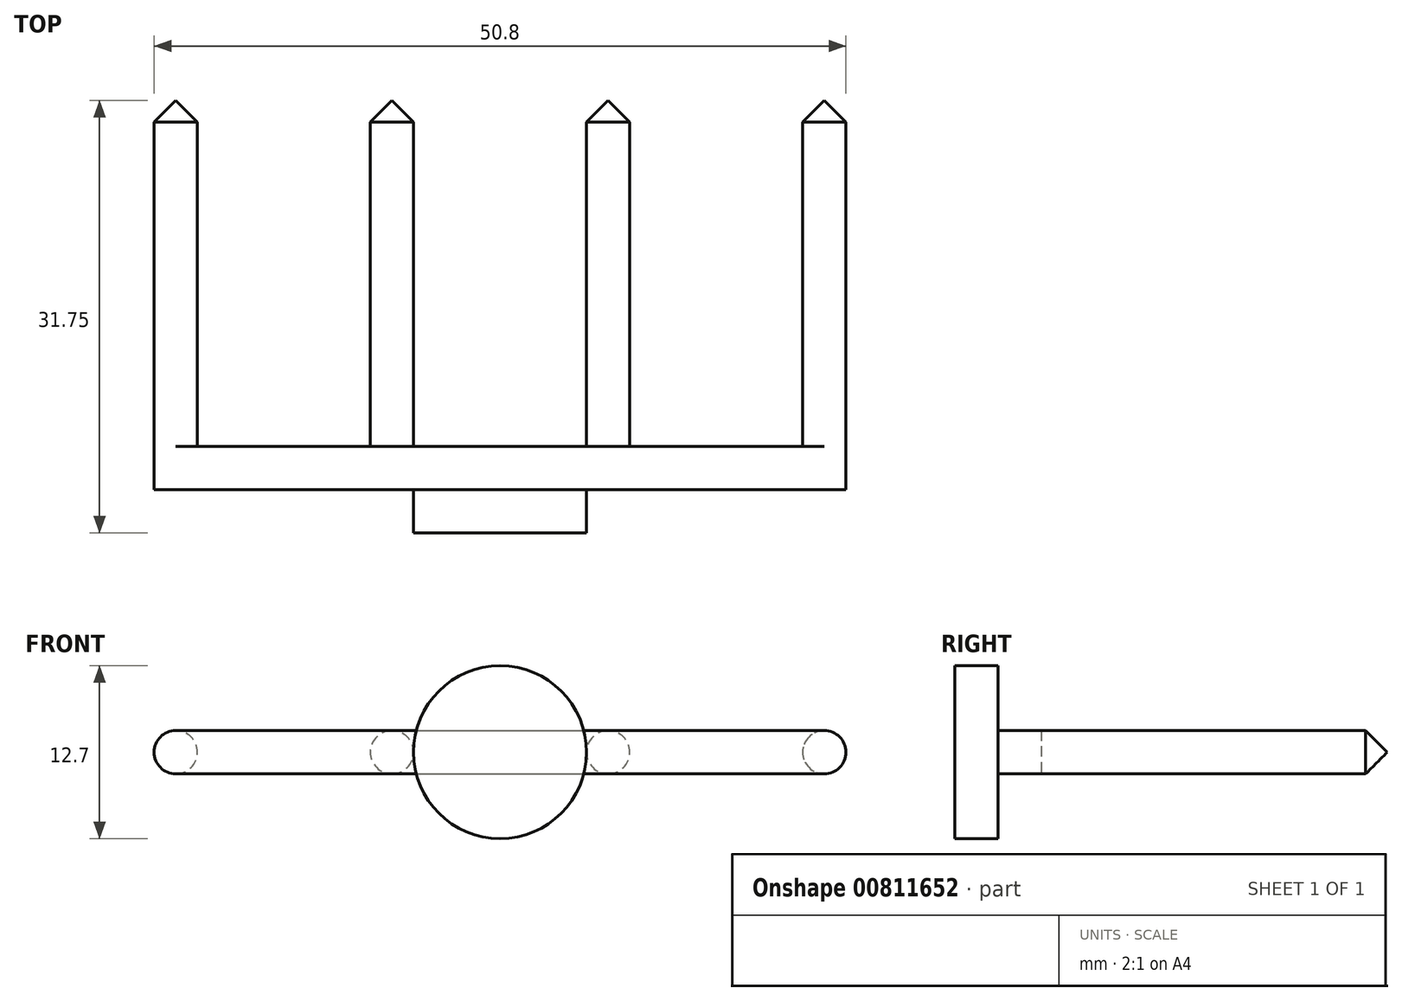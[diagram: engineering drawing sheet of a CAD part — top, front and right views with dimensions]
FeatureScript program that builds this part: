
annotation { "Feature Type Name" : "Feature", "Feature Type Description" : "" }
export const myFeature = defineFeature(function(context is Context, id is Id, definition is map)
    precondition{}
    {
        {
            var Q0;
            Q0=qCreatedBy(makeId("Top.planeOp"),FACE);
            var sketch = newSketch(context, id + "F0", { "sketchPlane" : qUnion([Q0])});
            skLineSegment(sketch, "E0.bottom", {"start": v(-14.88, 23.6) * mm, "end": v(-2.18, 23.6) * mm});
            skLineSegment(sketch, "E0.top", {"start": v(-14.88, 20.43) * mm, "end": v(-2.18, 20.43) * mm});
            skLineSegment(sketch, "E0.left", {"start": v(-14.88, 23.6) * mm, "end": v(-14.88, 20.43) * mm});
            skLineSegment(sketch, "E0.right", {"start": v(-2.18, 23.6) * mm, "end": v(-2.18, 20.43) * mm});
            skLineSegment(sketch, "E1", {"start": v(-2.18, 23.6) * mm, "end": v(16.87, 23.6) * mm});
            skLineSegment(sketch, "E2", {"start": v(-14.88, 23.6) * mm, "end": v(-33.93, 23.6) * mm});
            skLineSegment(sketch, "E3", {"start": v(-33.93, 23.6) * mm, "end": v(-33.93, 26.78) * mm});
            skLineSegment(sketch, "E4", {"start": v(-33.93, 26.78) * mm, "end": v(16.87, 26.78) * mm});
            skLineSegment(sketch, "E5", {"start": v(16.87, 26.78) * mm, "end": v(16.87, 23.6) * mm});
            skLineSegment(sketch, "E6", {"start": v(-33.93, 26.78) * mm, "end": v(-33.93, 52.18) * mm});
            skLineSegment(sketch, "E7", {"start": v(-33.93, 52.18) * mm, "end": v(-30.76, 52.18) * mm});
            skLineSegment(sketch, "E8", {"start": v(-30.76, 52.18) * mm, "end": v(-30.76, 26.78) * mm});
            skLineSegment(sketch, "E9", {"start": v(16.87, 26.78) * mm, "end": v(16.87, 52.18) * mm});
            skLineSegment(sketch, "E10", {"start": v(16.87, 52.18) * mm, "end": v(13.7, 52.18) * mm});
            skLineSegment(sketch, "E11", {"start": v(13.7, 52.18) * mm, "end": v(13.7, 26.78) * mm});
            skLineSegment(sketch, "E12", {"start": v(-30.76, 26.78) * mm, "end": v(-18.06, 26.78) * mm});
            skLineSegment(sketch, "E13", {"start": v(-18.06, 26.78) * mm, "end": v(-18.06, 52.18) * mm});
            skLineSegment(sketch, "E14", {"start": v(-18.06, 52.18) * mm, "end": v(-14.88, 52.18) * mm});
            skLineSegment(sketch, "E15", {"start": v(-14.88, 52.18) * mm, "end": v(-14.88, 26.78) * mm});
            skLineSegment(sketch, "E16", {"start": v(-14.88, 26.78) * mm, "end": v(-8.53, 26.78) * mm});
            skLineSegment(sketch, "E17", {"start": v(-8.53, 26.78) * mm, "end": v(-2.18, 26.78) * mm});
            skLineSegment(sketch, "E18", {"start": v(-2.18, 26.78) * mm, "end": v(-2.18, 52.18) * mm});
            skLineSegment(sketch, "E19", {"start": v(-2.18, 52.18) * mm, "end": v(1, 52.18) * mm});
            skLineSegment(sketch, "E20", {"start": v(1, 52.18) * mm, "end": v(1, 26.78) * mm});
            skLineSegment(sketch, "E21", {"start": v(-8.53, 23.6) * mm, "end": v(-8.53, 20.43) * mm});
            skSolve(sketch);
        }
        {
            var Q0;
            {var subQ0=sQuery(id+"F0.wireOp",EDGE,"E0.left");Q0=makeQuery(id+"F0.imprint","IMPRINT",FACE,{"disambiguationData":[TD([[makeQuery(id+"F0.imprint","IMPRINT",EDGE,{"derivedFrom":subQ0}),1.0]])]});}
            var Q1;
            Q1=sQuery(id+"F0.wireOp",EDGE,"E21");
            revolve(context, id + "F1", {"surfaceOperationType" : NewSurfaceOperationType.NEW, "entities" : qUnion([Q0]), "axis" : qUnion([Q1]), "revolveType" : RevolveType.FULL});
        }
        {
            var Q0;
            {var subQ11=sQuery(id+"F0.wireOp",EDGE,"E1");Q0=makeQuery(id+"F0.imprint","IMPRINT",FACE,{"disambiguationData":[TD([[makeQuery(id+"F0.imprint","IMPRINT",EDGE,{"derivedFrom":subQ11}),1.0]])]});}
            var Q1;
            {var subQ0=sQuery(id+"F0.wireOp",EDGE,"E6");Q1=makeQuery(id+"F0.imprint","IMPRINT",FACE,{"disambiguationData":[TD([[makeQuery(id+"F0.imprint","IMPRINT",EDGE,{"derivedFrom":subQ0}),-1.0]])]});}
            var Q2;
            {var subQ0=sQuery(id+"F0.wireOp",EDGE,"E13");Q2=makeQuery(id+"F0.imprint","IMPRINT",FACE,{"disambiguationData":[TD([[makeQuery(id+"F0.imprint","IMPRINT",EDGE,{"derivedFrom":subQ0}),-1.0]])]});}
            var Q3;
            {var subQ0=sQuery(id+"F0.wireOp",EDGE,"E18");Q3=makeQuery(id+"F0.imprint","IMPRINT",FACE,{"disambiguationData":[TD([[makeQuery(id+"F0.imprint","IMPRINT",EDGE,{"derivedFrom":subQ0}),-1.0]])]});}
            var Q4;
            {var subQ0=sQuery(id+"F0.wireOp",EDGE,"E9");Q4=makeQuery(id+"F0.imprint","IMPRINT",FACE,{"disambiguationData":[TD([[makeQuery(id+"F0.imprint","IMPRINT",EDGE,{"derivedFrom":subQ0}),1.0]])]});}
            extrude(context, id + "F2", {"entities" : qUnion([Q0, Q1, Q2, Q3, Q4]), "operationType" : NewBodyOperationType.ADD, "endBound" : BoundingType.SYMMETRIC, "depth" : 3.17 * mm, "offsetDistance" : 25.4 * mm});
        }
        {
            var Q0;
            Q0=makeQuery(id+"F2.opExtrude","CAP_EDGE",EDGE,{"disambiguationData":[OSD([sQuery(id+"F0.wireOp",EDGE,"E3"),sQuery(id+"F0.wireOp",EDGE,"E6")])],"isStart":false});
            var Q1;
            Q1=makeQuery(id+"F2.opExtrude","CAP_EDGE",EDGE,{"disambiguationData":[OSD([sQuery(id+"F0.wireOp",EDGE,"E3"),sQuery(id+"F0.wireOp",EDGE,"E6")])],"isStart":true});
            var Q2;
            Q2=makeQuery(id+"F2.opExtrude","CAP_EDGE",EDGE,{"disambiguationData":[OSD([sQuery(id+"F0.wireOp",EDGE,"E8")])],"isStart":false});
            var Q3;
            Q3=makeQuery(id+"F2.opExtrude","CAP_EDGE",EDGE,{"disambiguationData":[OSD([sQuery(id+"F0.wireOp",EDGE,"E8")])],"isStart":true});
            var Q4;
            Q4=makeQuery(id+"F2.opExtrude","CAP_EDGE",EDGE,{"disambiguationData":[OSD([sQuery(id+"F0.wireOp",EDGE,"E13")])],"isStart":false});
            var Q5;
            Q5=makeQuery(id+"F2.opExtrude","CAP_EDGE",EDGE,{"disambiguationData":[OSD([sQuery(id+"F0.wireOp",EDGE,"E13")])],"isStart":true});
            var Q6;
            Q6=makeQuery(id+"F2.opExtrude","CAP_EDGE",EDGE,{"disambiguationData":[OSD([sQuery(id+"F0.wireOp",EDGE,"E15")])],"isStart":false});
            var Q7;
            Q7=makeQuery(id+"F2.opExtrude","CAP_EDGE",EDGE,{"disambiguationData":[OSD([sQuery(id+"F0.wireOp",EDGE,"E15")])],"isStart":true});
            var Q8;
            Q8=makeQuery(id+"F2.opExtrude","CAP_EDGE",EDGE,{"disambiguationData":[OSD([sQuery(id+"F0.wireOp",EDGE,"E18")])],"isStart":false});
            var Q9;
            Q9=makeQuery(id+"F2.opExtrude","CAP_EDGE",EDGE,{"disambiguationData":[OSD([sQuery(id+"F0.wireOp",EDGE,"E18")])],"isStart":true});
            var Q10;
            Q10=makeQuery(id+"F2.opExtrude","CAP_EDGE",EDGE,{"disambiguationData":[OSD([sQuery(id+"F0.wireOp",EDGE,"E20")])],"isStart":true});
            var Q11;
            Q11=makeQuery(id+"F2.opExtrude","CAP_EDGE",EDGE,{"disambiguationData":[OSD([sQuery(id+"F0.wireOp",EDGE,"E20")])],"isStart":false});
            var Q12;
            Q12=makeQuery(id+"F2.opExtrude","CAP_EDGE",EDGE,{"disambiguationData":[OSD([sQuery(id+"F0.wireOp",EDGE,"E5"),sQuery(id+"F0.wireOp",EDGE,"E9")])],"isStart":true});
            var Q13;
            Q13=makeQuery(id+"F2.opExtrude","CAP_EDGE",EDGE,{"disambiguationData":[OSD([sQuery(id+"F0.wireOp",EDGE,"E5"),sQuery(id+"F0.wireOp",EDGE,"E9")])],"isStart":false});
            var Q14;
            Q14=makeQuery(id+"F2.opExtrude","CAP_EDGE",EDGE,{"disambiguationData":[OSD([sQuery(id+"F0.wireOp",EDGE,"E11")])],"isStart":false});
            var Q15;
            Q15=makeQuery(id+"F2.opExtrude","CAP_EDGE",EDGE,{"disambiguationData":[OSD([sQuery(id+"F0.wireOp",EDGE,"E11")])],"isStart":true});
            fillet(context, id + "F3", {"entities" : qUnion([Q0, Q1, Q2, Q3, Q4, Q5, Q6, Q7, Q8, Q9, Q10, Q11, Q12, Q13, Q14, Q15]), "radius" : 1.59 * mm, "tangentPropagation" : true, "allowEdgeOverflow" : false});
        }
        {
            var Q0;
            Q0=makeQuery(id+"F3.opFillet","BLEND_EDGE",EDGE,{"blendedFrom":[makeQuery(id+"F2.opExtrude","CAP_EDGE",EDGE,{"disambiguationData":[OSD([sQuery(id+"F0.wireOp",EDGE,"E3"),sQuery(id+"F0.wireOp",EDGE,"E6")])],"isStart":true}),makeQuery(id+"F2.opExtrude","SWEPT_FACE",FACE,{"disambiguationData":[OSD([sQuery(id+"F0.wireOp",EDGE,"E7")])]})],"blendedInto":[makeQuery(id+"F2.opExtrude","SWEPT_FACE",FACE,{"disambiguationData":[OSD([sQuery(id+"F0.wireOp",EDGE,"E7")])]})]});
            var Q1;
            Q1=makeQuery(id+"F3.opFillet","BLEND_EDGE",EDGE,{"blendedFrom":[makeQuery(id+"F2.opExtrude","CAP_EDGE",EDGE,{"disambiguationData":[OSD([sQuery(id+"F0.wireOp",EDGE,"E13")])],"isStart":true}),makeQuery(id+"F2.opExtrude","SWEPT_FACE",FACE,{"disambiguationData":[OSD([sQuery(id+"F0.wireOp",EDGE,"E14")])]})],"blendedInto":[makeQuery(id+"F2.opExtrude","SWEPT_FACE",FACE,{"disambiguationData":[OSD([sQuery(id+"F0.wireOp",EDGE,"E14")])]})]});
            var Q2;
            Q2=makeQuery(id+"F3.opFillet","BLEND_EDGE",EDGE,{"blendedFrom":[makeQuery(id+"F2.opExtrude","CAP_EDGE",EDGE,{"disambiguationData":[OSD([sQuery(id+"F0.wireOp",EDGE,"E18")])],"isStart":true}),makeQuery(id+"F2.opExtrude","SWEPT_FACE",FACE,{"disambiguationData":[OSD([sQuery(id+"F0.wireOp",EDGE,"E19")])]})],"blendedInto":[makeQuery(id+"F2.opExtrude","SWEPT_FACE",FACE,{"disambiguationData":[OSD([sQuery(id+"F0.wireOp",EDGE,"E19")])]})]});
            var Q3;
            Q3=makeQuery(id+"F3.opFillet","BLEND_EDGE",EDGE,{"blendedFrom":[makeQuery(id+"F2.opExtrude","CAP_EDGE",EDGE,{"disambiguationData":[OSD([sQuery(id+"F0.wireOp",EDGE,"E5"),sQuery(id+"F0.wireOp",EDGE,"E9")])],"isStart":true}),makeQuery(id+"F2.opExtrude","SWEPT_FACE",FACE,{"disambiguationData":[OSD([sQuery(id+"F0.wireOp",EDGE,"E10")])]})],"blendedInto":[makeQuery(id+"F2.opExtrude","SWEPT_FACE",FACE,{"disambiguationData":[OSD([sQuery(id+"F0.wireOp",EDGE,"E10")])]})]});
            chamfer(context, id + "F4", {"entities" : qUnion([Q0, Q1, Q2, Q3]), "width" : 1.59 * mm, "tangentPropagation" : true});
        }
    });
